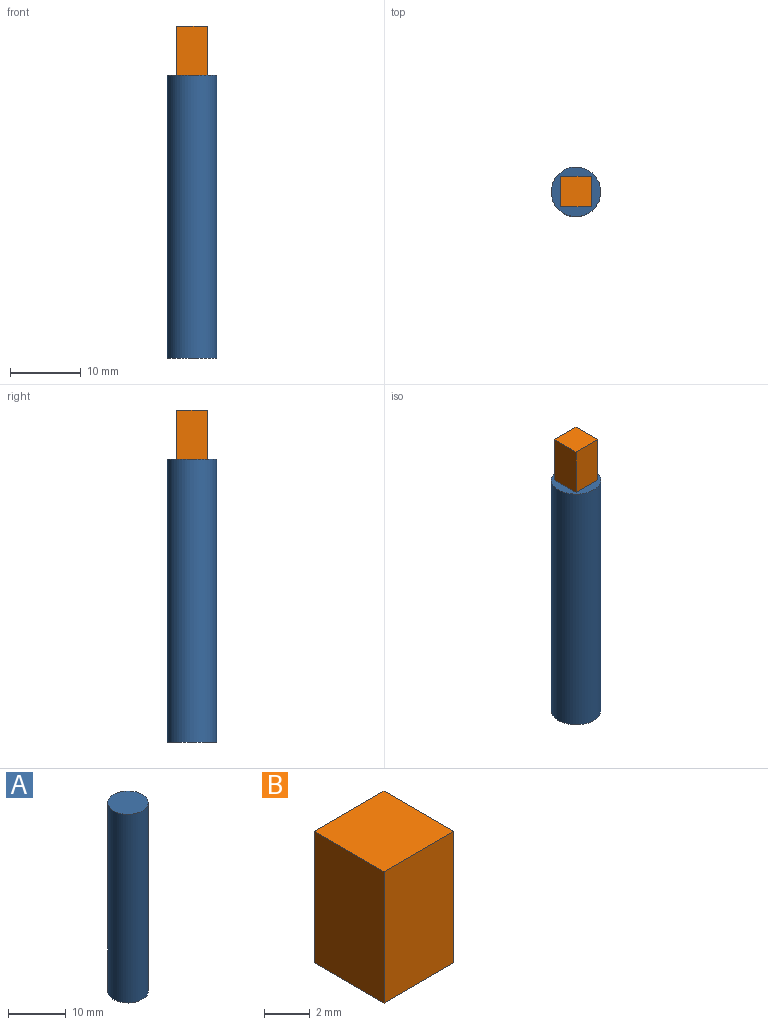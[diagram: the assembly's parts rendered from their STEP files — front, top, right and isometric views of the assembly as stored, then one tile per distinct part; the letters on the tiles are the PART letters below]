
ASSEMBLY  parts=2 mates=1
PART A: 3 faces, bbox 7x7x40 mm
  f0: cylinder r=3.5mm len=40mm, axis (0,0,-1), area 879.6mm2, adj f1,f2
  f1: plane 7x7mm, normal (0,0,1), area 38.5mm2, adj f0
  f2: plane 7x7mm, normal (0,0,-1), area 38.5mm2, adj f0
PART B: 6 faces, bbox 4.3x4.3x7 mm
  f0: plane 7x4.3mm, normal (0,-1,0), area 30.1mm2, adj f1,f3,f4,f5
  f1: plane 7x4.3mm, normal (1,0,0), area 30.1mm2, adj f0,f2,f4,f5
  f2: plane 7x4.3mm, normal (0,1,0), area 30.1mm2, adj f1,f3,f4,f5
  f3: plane 7x4.3mm, normal (-1,0,0), area 30.1mm2, adj f0,f2,f4,f5
  f4: plane 4.3x4.3mm, normal (0,0,1), area 18.5mm2, adj f0,f1,f2,f3
  f5: plane 4.3x4.3mm, normal (0,0,-1), area 18.5mm2, adj f0,f1,f2,f3
PLACE A t=(-8.14,-0.31,-13.42)mm
PLACE B rot(axis=(1,0,0),180deg) t=(-8.14,-0.31,33.58)mm
MATE fastened B.f4 <-> A.f0  axis (0,0,-1) through (-8.14,-0.31,26.58)mm
